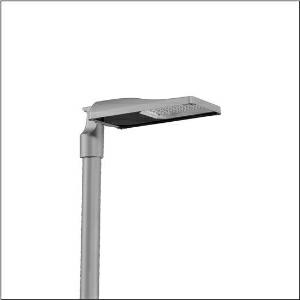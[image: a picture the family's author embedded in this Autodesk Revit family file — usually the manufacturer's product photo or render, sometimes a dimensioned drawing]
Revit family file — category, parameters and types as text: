
# Revit family: streetlight_sl_31_mini___st1_0a_5xh2d3aa08ja_eb00
name_source: partatom
category: Lighting Fixtures
units: mm (PartAtom-declared; Revit-internal decimal feet)

## family parameters
Cut with Voids When Loaded = No
Host = Face
Light Source = No
Part Type = Normal
Room Calculation Point = No
Round Connector Dimension = Use Diameter
Shared = No

## types (1)
- --- (1 x LED, 12140 lm, 81.1 W, 3000K)
    Apparent Load = 81 VA
    CIE Flux Codes = 40 73 97 100 100
    Color Rendering = 70
    Color Temperature = 3000K
    Default Elevation = 1800 mm
    Description = Streetlight SL 31 mini Easy mast luminaire for post-top, side-entry; light control with lens of PMMA; light distribution: ST1.0a, direct asymmetric distribution, for standard-compliant lighting for roads and squares; LED: luminous flux: 12.140lm, light colour: 730, colour temperature: 3000K; luminous efficacy: 149,7lm/W; control: overheat protection, intelligent temperature release in ECG and LED module, constant luminous flux control, time-dependent luminous flux control, flexible luminous flux parameterisation, pre-setting: linear dimming characteristic; luminaire housing, of diecast aluminium, Siteco® metallic grey (DB 702S), corrosivity category C5 high according to DIN EN ISO 12944; cover of toughened safety glass, transparent, mast flange of diecast aluminium, Siteco® metallic grey (DB 702S), spigot size: 76/60mm, mast flange included unmounted; with cable H07RN-F 2x 1.5mm², cable length: 10,5m, connection cable pre-assembled; mains connection: 220..240V, AC, 50/60Hz; power consumption (at start of service life): 81,1W / (at end of service life): 88,3W / (with reduced operation 50%): 36,4W; protection rating (complete): IP66; insulation class (complete): insulation class II (safety insulation); impact resistance: IK09; certification: CE, ENEC, ENEC+, VDE, UKCA; permissible operating ambient temperature for outdoor applications: -40..+50°C; packaging unit: 1 piece

Light Distribution: ST1.0a
    Height = 76 mm
    Lamp = 1 x LED
    Lamp Light Flux = 12140 lm
    Lamp Power = 81.1 W
    Lamp count = 1
    Length = 547 mm
    Luminous efficacy = 150 lm/W
    Manufacturer = Siteco
    ModVariant = No
    Model = 5XH2D3AA08JA
    Number of Poles = 1
    OnlyDefault = Yes
    Power Factor = 1
    Product Name = Streetlight SL 31 mini | ST1.0a
    Product group = mast luminaire | pylon top
    ProductGroupID = 6100
    Protection Class = Protection class II
    Protection Degree = IP 66
    RLX_Detail_Level = 1
    RLX_Emergency_Light_Flux = 0 lm
    RLX_Emergency_Type = 0
    RLX_Emergency_Type_DB = No
    RlxData = <blob elided: 39669 chars, md5=c7de56b1>
    Socket = socket
    Standby Power = 0 W
    System Light Flux = 12140 lm
    System Power = 81 W
    Type Comments = factory setting: luminous flux: 100 % | dim-lin: 254 | 860 mA
    Type Image = l_1300326.jpg
    URL = http://relux.com
    VarID = @adj_048054
    Voltage = 0 V
    Weight = 0.00 kg
    Width = 265 mm

## geometry (parser evidence)
native form markers: Blend x4, Sweep x11
no freeform markers — native parametric forms only
